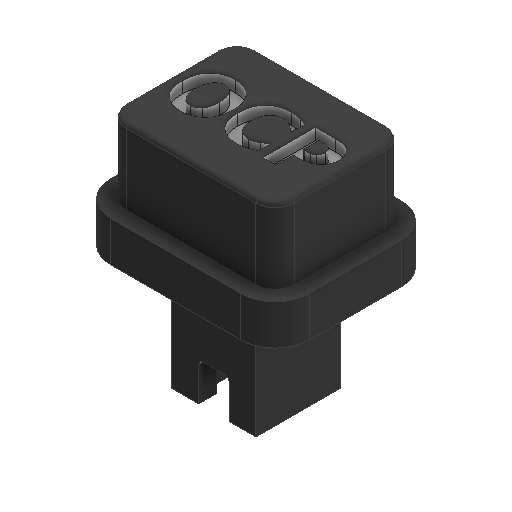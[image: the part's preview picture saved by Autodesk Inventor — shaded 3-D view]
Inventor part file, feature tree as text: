
AUTODESK INVENTOR PART (.ipt)
format: ipt  version: 2025 (Build 290162000, 162)  size: 376,832 bytes
history: native  units: mm
features: sketch x7, extrude x6, fillet x5, mirror x1, emboss x1, plane x1
ambient origin geometry x8: Origin, YZ Plane, XZ Plane, XY Plane, X Axis, Y Axis, Z Axis, Center Point
bodies: Solid1 (feature_tree)
feature tree (21):
  extrude  "Extrusion1"  Depth=6.0mm TaperAngle=0.0deg
  extrude  "Extrusion2"  Depth=2.8mm TaperAngle=0.0deg
  extrude  "Extrusion3"  Depth=2.0mm
  extrude  "Extrusion4"  Depth=0.1mm
  mirror  "Mirror1"
  extrude  "Extrusion5"  Depth=0.14mm
  fillet  "Fillet1"  [1 undecoded]
  fillet  "Fillet2"  Radius=6.8mm
  extrude  "Extrusion6"  Depth=6.0mm TaperAngle=0.0deg
  fillet  "Fillet3"  Radius=1.0mm
  fillet  "Fillet4"  Radius=0.2mm
  fillet  "Fillet5"  Radius=0.8mm
  emboss  "Emboss1"
  sketch  "Sketch1"  dims[d0=4.4mm d1=6.0mm d2=0.0mm]
  sketch  "Sketch2"  dims[d3=2.5mm d4=2.8mm d5=0.0mm]
  sketch  "Sketch3"  dims[d6=1.6mm d7=2.0mm]
  sketch  "Sketch4"  dims[d8=0.0mm d9=0.0mm d13=0.1mm]
  plane  "Work Plane1"
  sketch  "Sketch5"  dims[d14=1.9mm d15=0.14mm d16=0.0mm d17=0.0mm d18=6.8mm]
  sketch  "Sketch6"  dims[d19=8.8mm d20=6.0mm d21=0.0mm d22=1.0mm d23=0.2mm d24=0.8mm]
  sketch  "Sketch7"  dims[d25=2.1mm d26=0.0mm d27=0.6mm d28=30.0deg d29=0.105946mm d30=1.9mm d31=0.2mm d32=0.2mm d33=0.4mm d34=0.5mm d35=0.6mm d36=0.0mm d37=1.95mm]
note: 1 required parameter value undecoded (feature->parameter linkage not recoverable at this tier; creation-order binding heuristic only, values carry confidence <= 0.55)
